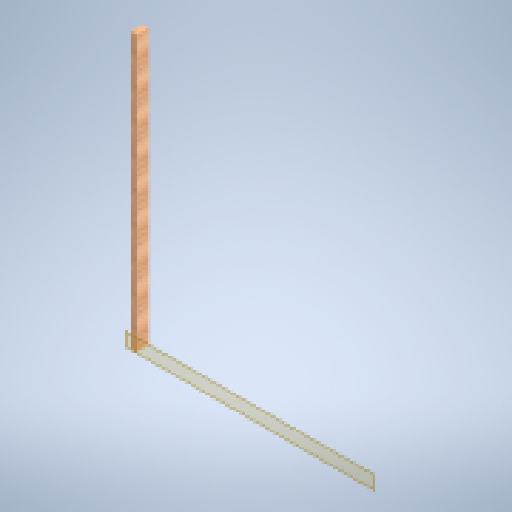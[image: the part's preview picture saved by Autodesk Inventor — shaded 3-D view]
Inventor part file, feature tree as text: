
AUTODESK INVENTOR PART (.ipt)
format: ipt  version: 2025 (Build 290162000, 162)  size: 140,800 bytes
history: native  units: in
note: dims shown in document units (in); Inventor stores cm internally (conversion verified against a paired STEP export)
features: other x5, reference x3, plane x1, extrude x1, sketch x1
ambient origin geometry x8: Origin, YZ Plane, XZ Plane, XY Plane, X Axis, Y Axis, Z Axis, Center Point
bodies: Solid1 (feature_tree)
feature tree (11):
  plane  "Work Plane1"
  extrude  "Extrusion1"  [1 undecoded]
  sketch  "Sketch1"  dims[d0=4.0in d1=0.0in]
  reference  "Reference1"
  reference  "Reference2"
  reference  "Reference3"
  other  "<userpath>\Documents\GitHub\USCTigerBurn24\v2\Tiger.iam"
  other  "Tiger.iam"
  other  "2x4x76:7"
  other  "2X4X65.191:4"
  other  "2x4x76:5"
note: 1 required parameter value undecoded (feature->parameter linkage not recoverable at this tier; creation-order binding heuristic only, values carry confidence <= 0.55)
